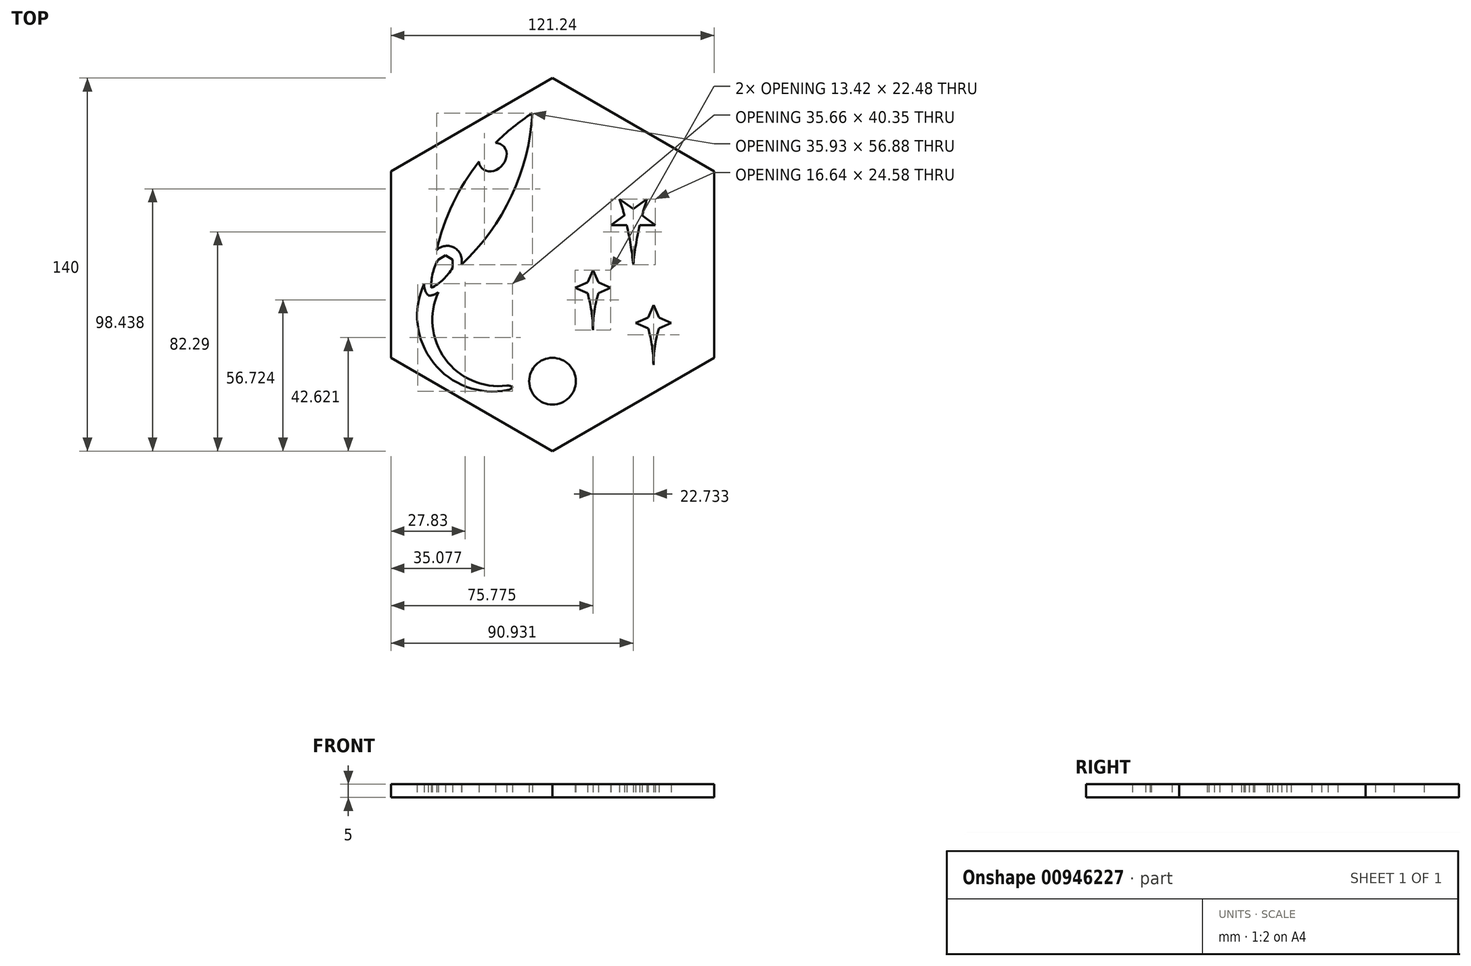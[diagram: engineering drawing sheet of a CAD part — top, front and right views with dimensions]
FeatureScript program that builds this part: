
annotation { "Feature Type Name" : "Feature", "Feature Type Description" : "" }
export const myFeature = defineFeature(function(context is Context, id is Id, definition is map)
    precondition{}
    {
        {
            var Q0;
            Q0=qCreatedBy(makeId("Top.planeOp"),FACE);
            var sketch = newSketch(context, id + "F0", { "sketchPlane" : qUnion([Q0])});
            skCircle(sketch, "E0.cCircle", {"center": v(0, 0) * mm, "radius": 60.62 * mm, "construction": true});
            skLineSegment(sketch, "E0.0", {"start": v(60.62, 35) * mm, "end": v(60.62, -35) * mm});
            skLineSegment(sketch, "E0.1", {"start": v(60.62, -35) * mm, "end": v(0, -70) * mm});
            skLineSegment(sketch, "E0.2", {"start": v(0, -70) * mm, "end": v(-60.62, -35) * mm});
            skLineSegment(sketch, "E0.3", {"start": v(-60.62, -35) * mm, "end": v(-60.62, 35) * mm});
            skLineSegment(sketch, "E0.4", {"start": v(-60.62, 35) * mm, "end": v(0, 70) * mm});
            skLineSegment(sketch, "E0.5", {"start": v(0, 70) * mm, "end": v(60.62, 35) * mm});
            skPoint(sketch, "E0.0.midPoint", {"position": v(60.62, 0) * mm});
            skLineSegment(sketch, "E1", {"start": v(0, 0) * mm, "end": v(0, -35) * mm, "construction": true});
            skLineSegment(sketch, "E2", {"start": v(-30.31, 17.5) * mm, "end": v(-60.62, 35) * mm, "construction": true});
            skLineSegment(sketch, "E3", {"start": v(0, 0) * mm, "end": v(60.62, 35) * mm, "construction": true});
            skLineSegment(sketch, "E4", {"start": v(60.62, -35) * mm, "end": v(15.16, -8.75) * mm, "construction": true});
            skLineSegment(sketch, "E5", {"start": v(0, -35) * mm, "end": v(30.31, 17.5) * mm, "construction": true});
            skLineSegment(sketch, "E6", {"start": v(0, -35) * mm, "end": v(0, -43.75) * mm, "construction": true});
            skLineSegment(sketch, "E7", {"start": v(0, -52.5) * mm, "end": v(0, -70) * mm, "construction": true});
            skLineSegment(sketch, "E8", {"start": v(0, -43.75) * mm, "end": v(0, -52.5) * mm, "construction": true});
            skCircle(sketch, "E9", {"center": v(0, -43.75) * mm, "radius": 8.75 * mm});
            skPoint(sketch, "E10", {"position": v(37.89, -21.88) * mm});
            skPoint(sketch, "E11", {"position": v(-30.31, 17.5) * mm});
            skLineSegment(sketch, "E12", {"start": v(-60.62, -35) * mm, "end": v(-45.47, -8.75) * mm, "construction": true});
            skLineSegment(sketch, "E13", {"start": v(0, 70) * mm, "end": v(-7.58, 56.88) * mm, "construction": true});
            skLineSegment(sketch, "E14", {"start": v(-45.47, -8.75) * mm, "end": v(-37.89, 4.37) * mm, "construction": true});
            skLineSegment(sketch, "E15", {"start": v(-15.16, 43.75) * mm, "end": v(-30.31, 17.5) * mm, "construction": true});
            skLineSegment(sketch, "E16", {"start": v(-7.58, 56.88) * mm, "end": v(-15.16, 43.75) * mm, "construction": true});
            skArc(sketch, "E17", {"start": v(-60.62, -16.52) * mm, "mid": v(-59.59, -16.11) * mm, "end": v(-58.56, -15.69) * mm, "construction": true});
            skLineSegment(sketch, "E18", {"start": v(-15.16, 8.75) * mm, "end": v(-30.31, 17.5) * mm, "construction": true});
            skLineSegment(sketch, "E19", {"start": v(0, 0) * mm, "end": v(-15.16, 8.75) * mm, "construction": true});
            skPoint(sketch, "E20", {"position": v(-22.73, 13.12) * mm});
            skArc(sketch, "E21.trimOffspring", {"start": v(-45.47, -8.75) * mm, "mid": v(-18.65, 19.52) * mm, "end": v(-7.58, 56.88) * mm});
            skArc(sketch, "E22.MirrorCS", {"start": v(-45.47, -8.75) * mm, "mid": v(-34.4, 28.6) * mm, "end": v(-7.58, 56.88) * mm});
            skLineSegment(sketch, "E23", {"start": v(-37.89, 4.37) * mm, "end": v(-34.1, 10.94) * mm, "construction": true});
            skLineSegment(sketch, "E24", {"start": v(-34.1, 10.94) * mm, "end": v(-30.31, 17.5) * mm, "construction": true});
            skCircle(sketch, "E25.cCircle", {"center": v(30.31, 17.5) * mm, "radius": 2.7 * mm, "construction": true});
            skLineSegment(sketch, "E25.0", {"start": v(35.45, 24.58) * mm, "end": v(30.31, 8.75) * mm});
            skLineSegment(sketch, "E25.1", {"start": v(38.63, 14.8) * mm, "end": v(21.99, 14.8) * mm});
            skLineSegment(sketch, "E25.2", {"start": v(30.31, 8.75) * mm, "end": v(25.17, 24.58) * mm});
            skLineSegment(sketch, "E25.3", {"start": v(21.99, 14.8) * mm, "end": v(35.45, 24.58) * mm});
            skLineSegment(sketch, "E25.4", {"start": v(25.17, 24.58) * mm, "end": v(38.63, 14.8) * mm});
            skPoint(sketch, "E25.0.midPoint", {"position": v(32.88, 16.66) * mm});
            skPoint(sketch, "E26.orphan", {"position": v(27.13, 18.53) * mm});
            skPoint(sketch, "E27.orphan", {"position": v(30.31, 20.84) * mm});
            skPoint(sketch, "E28.orphan", {"position": v(33.49, 18.53) * mm});
            skPoint(sketch, "E29.orphan", {"position": v(32.28, 14.8) * mm});
            skPoint(sketch, "E30.orphan", {"position": v(28.35, 14.8) * mm});
            skLineSegment(sketch, "E31", {"start": v(30.31, 17.5) * mm, "end": v(30.31, 0) * mm, "construction": true});
            skPoint(sketch, "E32", {"position": v(30.31, 8.75) * mm});
            skArc(sketch, "E33", {"start": v(30.31, 0) * mm, "mid": v(28.4, 12.43) * mm, "end": v(25.17, 24.58) * mm});
            skArc(sketch, "E34", {"start": v(35.45, 24.58) * mm, "mid": v(32.22, 12.43) * mm, "end": v(30.31, 0) * mm});
            skLineSegment(sketch, "E35", {"start": v(30.31, 17.5) * mm, "end": v(27.97, 18.85) * mm, "construction": true});
            skCircle(sketch, "E36", {"center": v(30.31, 17.5) * mm, "radius": 1.35 * mm, "construction": true});
            skPoint(sketch, "E37", {"position": v(29.14, 18.18) * mm});
            skCircle(sketch, "E38", {"center": v(30.31, 17.5) * mm, "radius": 2.03 * mm, "construction": true});
            skLineSegment(sketch, "E39", {"start": v(30.31, 17.5) * mm, "end": v(30.99, 18.67) * mm, "construction": true});
            skLineSegment(sketch, "E40", {"start": v(30.99, 18.67) * mm, "end": v(31.66, 19.84) * mm, "construction": true});
            skPoint(sketch, "E41", {"position": v(31.32, 19.26) * mm});
            skSolve(sketch);
        }
        {
            var Q0;
            Q0=qCreatedBy(makeId("Top.planeOp"),FACE);
            var sketch = newSketch(context, id + "F1", { "sketchPlane" : qUnion([Q0])});
            skPoint(sketch, "E42.0", {"position": v(15.16, -8.75) * mm});
            skLineSegment(sketch, "E43.0", {"start": v(0, -70) * mm, "end": v(-60.62, -35) * mm});
            skLineSegment(sketch, "E44.0", {"start": v(-60.62, -35) * mm, "end": v(-60.62, 35) * mm});
            skLineSegment(sketch, "E45.0", {"start": v(-60.62, 35) * mm, "end": v(0, 70) * mm});
            skLineSegment(sketch, "E46.0", {"start": v(0, 70) * mm, "end": v(60.62, 35) * mm});
            skLineSegment(sketch, "E47.0", {"start": v(60.62, 35) * mm, "end": v(60.62, -35) * mm});
            skLineSegment(sketch, "E48.0", {"start": v(60.62, -35) * mm, "end": v(0, -70) * mm});
            skArc(sketch, "E49.0", {"start": v(-45.47, -8.75) * mm, "mid": v(-18.65, 19.52) * mm, "end": v(-7.58, 56.88) * mm});
            skArc(sketch, "E50.0", {"start": v(-45.47, -8.75) * mm, "mid": v(-34.4, 28.6) * mm, "end": v(-7.58, 56.88) * mm});
            skCircle(sketch, "E51.cCircle", {"center": v(15.16, -8.75) * mm, "radius": 2.03 * mm, "construction": true});
            skLineSegment(sketch, "E51.3", {"start": v(13.13, -6.72) * mm, "end": v(17.18, -6.72) * mm});
            skPoint(sketch, "E51.0.midPoint", {"position": v(17.18, -8.75) * mm});
            skCircle(sketch, "E52.cCircle", {"center": v(15.16, -5.55) * mm, "radius": 1.17 * mm, "construction": true});
            skLineSegment(sketch, "E52.1", {"start": v(13.13, -6.72) * mm, "end": v(15.16, -3.2) * mm});
            skLineSegment(sketch, "E52.2", {"start": v(15.16, -3.2) * mm, "end": v(17.18, -6.72) * mm});
            skPoint(sketch, "E52.0.midPoint", {"position": v(15.16, -6.72) * mm});
            skLineSegment(sketch, "E53", {"start": v(15.16, -5.55) * mm, "end": v(15.16, -0.87) * mm, "construction": true});
            skPoint(sketch, "E54", {"position": v(15.16, -3.2) * mm});
            skLineSegment(sketch, "E55", {"start": v(15.16, -3.2) * mm, "end": v(15.16, -0.87) * mm, "construction": true});
            skLineSegment(sketch, "E56", {"start": v(17.18, -6.72) * mm, "end": v(15.16, -2.04) * mm});
            skLineSegment(sketch, "E57", {"start": v(13.13, -6.72) * mm, "end": v(15.16, -2.04) * mm});
            skLineSegment(sketch, "E58.1.0", {"start": v(13.13, -6.72) * mm, "end": v(8.44, -8.75) * mm});
            skPoint(sketch, "E58.1.1", {"position": v(13.13, -8.75) * mm});
            skLineSegment(sketch, "E58.1.2", {"start": v(9.62, -8.75) * mm, "end": v(13.13, -6.72) * mm});
            skLineSegment(sketch, "E58.1.3", {"start": v(9.62, -8.75) * mm, "end": v(7.27, -8.75) * mm, "construction": true});
            skLineSegment(sketch, "E58.1.4", {"start": v(11.96, -8.75) * mm, "end": v(7.27, -8.75) * mm, "construction": true});
            skLineSegment(sketch, "E58.1.5", {"start": v(13.13, -10.78) * mm, "end": v(8.44, -8.75) * mm});
            skLineSegment(sketch, "E58.1.6", {"start": v(13.13, -10.78) * mm, "end": v(13.13, -6.72) * mm});
            skCircle(sketch, "E58.1.7", {"center": v(11.96, -8.75) * mm, "radius": 1.17 * mm, "construction": true});
            skPoint(sketch, "E58.1.8", {"position": v(9.62, -8.75) * mm});
            skLineSegment(sketch, "E58.1.9", {"start": v(13.13, -10.78) * mm, "end": v(9.62, -8.75) * mm});
            skLineSegment(sketch, "E58.2.0", {"start": v(13.13, -10.78) * mm, "end": v(15.16, -15.46) * mm});
            skPoint(sketch, "E58.2.1", {"position": v(15.16, -10.78) * mm});
            skLineSegment(sketch, "E58.2.2", {"start": v(15.16, -14.3) * mm, "end": v(13.13, -10.78) * mm});
            skLineSegment(sketch, "E58.2.3", {"start": v(15.16, -14.3) * mm, "end": v(15.16, -16.63) * mm, "construction": true});
            skLineSegment(sketch, "E58.2.4", {"start": v(15.16, -11.95) * mm, "end": v(15.16, -16.63) * mm, "construction": true});
            skLineSegment(sketch, "E58.2.5", {"start": v(17.18, -10.78) * mm, "end": v(15.16, -15.46) * mm});
            skLineSegment(sketch, "E58.2.6", {"start": v(17.18, -10.78) * mm, "end": v(13.13, -10.78) * mm});
            skCircle(sketch, "E58.2.7", {"center": v(15.16, -11.95) * mm, "radius": 1.17 * mm, "construction": true});
            skPoint(sketch, "E58.2.8", {"position": v(15.16, -14.3) * mm});
            skLineSegment(sketch, "E58.2.9", {"start": v(17.18, -10.78) * mm, "end": v(15.16, -14.3) * mm});
            skLineSegment(sketch, "E58.3.0", {"start": v(17.18, -10.78) * mm, "end": v(21.87, -8.75) * mm});
            skLineSegment(sketch, "E58.3.2", {"start": v(20.7, -8.75) * mm, "end": v(17.18, -10.78) * mm});
            skLineSegment(sketch, "E58.3.3", {"start": v(20.7, -8.75) * mm, "end": v(23.04, -8.75) * mm, "construction": true});
            skLineSegment(sketch, "E58.3.4", {"start": v(18.35, -8.75) * mm, "end": v(23.04, -8.75) * mm, "construction": true});
            skLineSegment(sketch, "E58.3.5", {"start": v(17.18, -6.72) * mm, "end": v(21.87, -8.75) * mm});
            skLineSegment(sketch, "E58.3.6", {"start": v(17.18, -6.72) * mm, "end": v(17.18, -10.78) * mm});
            skCircle(sketch, "E58.3.7", {"center": v(18.35, -8.75) * mm, "radius": 1.17 * mm, "construction": true});
            skPoint(sketch, "E58.3.8", {"position": v(20.7, -8.75) * mm});
            skLineSegment(sketch, "E58.3.9", {"start": v(17.18, -6.72) * mm, "end": v(20.7, -8.75) * mm});
            skLineSegment(sketch, "E59", {"start": v(15.16, -8.75) * mm, "end": v(15.16, -24.51) * mm, "construction": true});
            skArc(sketch, "E60", {"start": v(17.18, -10.78) * mm, "mid": v(15.67, -17.57) * mm, "end": v(15.16, -24.51) * mm});
            skArc(sketch, "E61", {"start": v(15.16, -24.51) * mm, "mid": v(14.65, -17.57) * mm, "end": v(13.13, -10.78) * mm});
            skPoint(sketch, "E62.0", {"position": v(37.89, -21.88) * mm});
            skCircle(sketch, "E63.cCircle", {"center": v(37.89, -21.88) * mm, "radius": 2.03 * mm, "construction": true});
            skLineSegment(sketch, "E63.0", {"start": v(39.92, -19.85) * mm, "end": v(39.92, -23.9) * mm});
            skLineSegment(sketch, "E63.1", {"start": v(39.92, -23.9) * mm, "end": v(35.86, -23.9) * mm});
            skLineSegment(sketch, "E63.2", {"start": v(35.86, -23.9) * mm, "end": v(35.86, -19.85) * mm});
            skLineSegment(sketch, "E63.3", {"start": v(35.86, -19.85) * mm, "end": v(39.92, -19.85) * mm});
            skPoint(sketch, "E63.0.midPoint", {"position": v(39.92, -21.88) * mm});
            skCircle(sketch, "E64.cCircle", {"center": v(37.89, -18.68) * mm, "radius": 1.17 * mm, "construction": true});
            skLineSegment(sketch, "E64.0", {"start": v(35.86, -19.85) * mm, "end": v(37.89, -16.33) * mm});
            skLineSegment(sketch, "E64.1", {"start": v(37.89, -16.33) * mm, "end": v(39.92, -19.85) * mm});
            skLineSegment(sketch, "E64.2", {"start": v(39.92, -19.85) * mm, "end": v(35.86, -19.85) * mm});
            skPoint(sketch, "E64.0.midPoint", {"position": v(36.87, -18.1) * mm});
            skLineSegment(sketch, "E65", {"start": v(37.89, -18.68) * mm, "end": v(37.89, -14) * mm, "construction": true});
            skLineSegment(sketch, "E66", {"start": v(37.89, -16.33) * mm, "end": v(37.89, -14) * mm, "construction": true});
            skLineSegment(sketch, "E67", {"start": v(39.92, -19.85) * mm, "end": v(37.89, -15.16) * mm});
            skLineSegment(sketch, "E68", {"start": v(35.86, -19.85) * mm, "end": v(37.89, -15.16) * mm});
            skLineSegment(sketch, "E69.1.0", {"start": v(35.86, -23.9) * mm, "end": v(32.35, -21.87) * mm});
            skLineSegment(sketch, "E69.1.1", {"start": v(34.69, -21.87) * mm, "end": v(30, -21.88) * mm, "construction": true});
            skLineSegment(sketch, "E69.1.2", {"start": v(32.35, -21.88) * mm, "end": v(35.86, -19.85) * mm});
            skLineSegment(sketch, "E69.1.3", {"start": v(32.35, -21.88) * mm, "end": v(30, -21.88) * mm, "construction": true});
            skLineSegment(sketch, "E69.1.4", {"start": v(35.86, -23.9) * mm, "end": v(31.18, -21.88) * mm});
            skPoint(sketch, "E69.1.5", {"position": v(34.1, -22.89) * mm});
            skLineSegment(sketch, "E69.1.6", {"start": v(35.86, -19.85) * mm, "end": v(35.86, -23.9) * mm});
            skCircle(sketch, "E69.1.7", {"center": v(34.69, -21.87) * mm, "radius": 1.17 * mm, "construction": true});
            skLineSegment(sketch, "E69.1.8", {"start": v(35.86, -19.85) * mm, "end": v(31.18, -21.88) * mm});
            skLineSegment(sketch, "E69.2.0", {"start": v(39.92, -23.9) * mm, "end": v(37.89, -27.42) * mm});
            skLineSegment(sketch, "E69.2.1", {"start": v(37.89, -25.07) * mm, "end": v(37.89, -29.76) * mm, "construction": true});
            skLineSegment(sketch, "E69.2.2", {"start": v(37.89, -27.42) * mm, "end": v(35.86, -23.9) * mm});
            skLineSegment(sketch, "E69.2.3", {"start": v(37.89, -27.42) * mm, "end": v(37.89, -29.76) * mm, "construction": true});
            skLineSegment(sketch, "E69.2.4", {"start": v(39.92, -23.9) * mm, "end": v(37.89, -28.59) * mm});
            skPoint(sketch, "E69.2.5", {"position": v(38.9, -25.66) * mm});
            skLineSegment(sketch, "E69.2.6", {"start": v(35.86, -23.9) * mm, "end": v(39.92, -23.9) * mm});
            skCircle(sketch, "E69.2.7", {"center": v(37.89, -25.07) * mm, "radius": 1.17 * mm, "construction": true});
            skLineSegment(sketch, "E69.2.8", {"start": v(35.86, -23.9) * mm, "end": v(37.89, -28.59) * mm});
            skLineSegment(sketch, "E69.3.0", {"start": v(39.92, -19.85) * mm, "end": v(43.43, -21.88) * mm});
            skLineSegment(sketch, "E69.3.1", {"start": v(41.09, -21.88) * mm, "end": v(45.77, -21.87) * mm, "construction": true});
            skLineSegment(sketch, "E69.3.2", {"start": v(43.43, -21.87) * mm, "end": v(39.92, -23.9) * mm});
            skLineSegment(sketch, "E69.3.3", {"start": v(43.43, -21.87) * mm, "end": v(45.77, -21.87) * mm, "construction": true});
            skLineSegment(sketch, "E69.3.4", {"start": v(39.92, -19.85) * mm, "end": v(44.6, -21.88) * mm});
            skPoint(sketch, "E69.3.5", {"position": v(41.67, -20.86) * mm});
            skLineSegment(sketch, "E69.3.6", {"start": v(39.92, -23.9) * mm, "end": v(39.92, -19.85) * mm});
            skCircle(sketch, "E69.3.7", {"center": v(41.09, -21.88) * mm, "radius": 1.17 * mm, "construction": true});
            skLineSegment(sketch, "E69.3.8", {"start": v(39.92, -23.9) * mm, "end": v(44.6, -21.87) * mm});
            skLineSegment(sketch, "E70", {"start": v(37.89, -21.88) * mm, "end": v(37.89, -37.64) * mm, "construction": true});
            skSolve(sketch);
        }
        {
            var Q0;
            Q0=makeQuery(id+"F0.imprint","IMPRINT",FACE,{"disambiguationData":[TD([[makeQuery(id+"F0.imprint","IMPRINT",EDGE,{"derivedFrom":sQuery(id+"F0.wireOp",EDGE,"E0.0")}),-1.0]])]});
            var sketch = newSketch(context, id + "F2", { "sketchPlane" : qUnion([Q0])});
            skPoint(sketch, "E71.0", {"position": v(35.86, -23.9) * mm});
            skPoint(sketch, "E72.0", {"position": v(39.92, -23.9) * mm});
            skPoint(sketch, "E73.0", {"position": v(37.89, -37.64) * mm});
            skArc(sketch, "E74", {"start": v(37.89, -37.64) * mm, "mid": v(37.38, -30.7) * mm, "end": v(35.86, -23.9) * mm});
            skLineSegment(sketch, "E75.0", {"start": v(37.89, -21.88) * mm, "end": v(37.89, -37.64) * mm, "construction": true});
            skArc(sketch, "E76", {"start": v(39.92, -23.9) * mm, "mid": v(38.4, -30.7) * mm, "end": v(37.89, -37.64) * mm});
            skSolve(sketch);
        }
        {
            var Q0;
            Q0=makeQuery(id+"F0.imprint","IMPRINT",FACE,{"disambiguationData":[TD([[makeQuery(id+"F0.imprint","IMPRINT",EDGE,{"derivedFrom":sQuery(id+"F0.wireOp",EDGE,"E0.0")}),-1.0]])]});
            var sketch = newSketch(context, id + "F3", { "sketchPlane" : qUnion([Q0])});
            skArc(sketch, "E77.0", {"start": v(-43.5, 5.36) * mm, "mid": v(-30.57, 34.63) * mm, "end": v(-7.58, 56.88) * mm});
            skArc(sketch, "E77.1", {"start": v(-34.23, 0) * mm, "mid": v(-15.35, 25.84) * mm, "end": v(-7.58, 56.88) * mm});
            skArc(sketch, "E78", {"start": v(-34.23, 0) * mm, "mid": v(-36.78, 6.3) * mm, "end": v(-43.5, 5.36) * mm});
            skLineSegment(sketch, "E79", {"start": v(-34.23, 0) * mm, "end": v(-36.55, 1.34) * mm, "construction": true});
            skLineSegment(sketch, "E80", {"start": v(-38.87, 2.68) * mm, "end": v(-43.5, 5.36) * mm, "construction": true});
            skLineSegment(sketch, "E81", {"start": v(-36.55, 1.34) * mm, "end": v(-38.87, 2.68) * mm, "construction": true});
            skLineSegment(sketch, "E82", {"start": v(-38.87, 2.68) * mm, "end": v(-40.2, 0.36) * mm, "construction": true});
            skPoint(sketch, "E83.orphan", {"position": v(-45.47, -8.75) * mm});
            skCircle(sketch, "E84.cCircle", {"center": v(-40.2, 0.36) * mm, "radius": 2.68 * mm, "construction": true});
            skLineSegment(sketch, "E84.2", {"start": v(-42.89, 1.9) * mm, "end": v(-40.2, 3.45) * mm});
            skLineSegment(sketch, "E84.3", {"start": v(-40.2, 3.45) * mm, "end": v(-37.53, 1.9) * mm});
            skLineSegment(sketch, "E84.4", {"start": v(-37.53, 1.9) * mm, "end": v(-37.53, -1.19) * mm});
            skPoint(sketch, "E84.0.midPoint", {"position": v(-41.55, -1.96) * mm});
            skArc(sketch, "E85", {"start": v(-45.47, -8.75) * mm, "mid": v(-40.95, -5.54) * mm, "end": v(-37.53, -1.19) * mm});
            skArc(sketch, "E86.MirrorCS", {"start": v(-45.47, -8.75) * mm, "mid": v(-44.94, -3.24) * mm, "end": v(-42.89, 1.9) * mm});
            skLineSegment(sketch, "E87", {"start": v(-36.22, 1.9) * mm, "end": v(-42.37, -8.75) * mm, "construction": true});
            skLineSegment(sketch, "E88", {"start": v(-35.74, 1.9) * mm, "end": v(-41.9, -8.75) * mm, "construction": true});
            skCircle(sketch, "E89.0", {"center": v(0, -43.75) * mm, "radius": 8.75 * mm});
            skLineSegment(sketch, "E90", {"start": v(0, -43.75) * mm, "end": v(-8.75, -43.75) * mm, "construction": true});
            skLineSegment(sketch, "E91", {"start": v(-17.5, -43.75) * mm, "end": v(-8.75, -43.75) * mm, "construction": true});
            skPoint(sketch, "E92", {"position": v(-44.94, -3.24) * mm});
            skPoint(sketch, "E93", {"position": v(-40.95, -5.54) * mm});
            skLineSegment(sketch, "E94", {"start": v(-48.15, -7.2) * mm, "end": v(-45.47, -8.75) * mm, "construction": true});
            skLineSegment(sketch, "E95", {"start": v(-37.53, -1.19) * mm, "end": v(-42.79, -10.3) * mm, "construction": true});
            skLineSegment(sketch, "E96", {"start": v(0, -43.75) * mm, "end": v(0, -52.5) * mm, "construction": true});
            skLineSegment(sketch, "E97", {"start": v(0, -43.75) * mm, "end": v(-6.19, -49.94) * mm, "construction": true});
            skLineSegment(sketch, "E98", {"start": v(0, -52.5) * mm, "end": v(-8.75, -43.75) * mm, "construction": true});
            skPoint(sketch, "E99", {"position": v(-4.38, -48.13) * mm});
            skLineSegment(sketch, "E100", {"start": v(0, -43.75) * mm, "end": v(-16.17, -50.45) * mm, "construction": true});
            skLineSegment(sketch, "E101", {"start": v(-6.19, -49.94) * mm, "end": v(-8.75, -43.75) * mm, "construction": true});
            skPoint(sketch, "E102", {"position": v(-7.47, -46.84) * mm});
            skCircle(sketch, "E103", {"center": v(0, -43.75) * mm, "radius": 17.5 * mm, "construction": true});
            skLineSegment(sketch, "E104", {"start": v(-16.17, -50.45) * mm, "end": v(-16.83, -47.1) * mm, "construction": true});
            skPoint(sketch, "E105", {"position": v(-16.83, -47.1) * mm});
            skLineSegment(sketch, "E106", {"start": v(0, -43.75) * mm, "end": v(-12.63, -46.26) * mm, "construction": true});
            skLineSegment(sketch, "E107", {"start": v(-45.47, -8.75) * mm, "end": v(-44.94, -3.24) * mm, "construction": true});
            skLineSegment(sketch, "E108", {"start": v(-40.95, -5.54) * mm, "end": v(-45.47, -8.75) * mm, "construction": true});
            skPoint(sketch, "E109", {"position": v(-45.2, -6) * mm});
            skPoint(sketch, "E110", {"position": v(-43.2, -7.15) * mm});
            skLineSegment(sketch, "E111", {"start": v(-13.13, -43.75) * mm, "end": v(-12.63, -46.26) * mm, "construction": true});
            skPoint(sketch, "E112.0", {"position": v(-15.16, 43.75) * mm});
            skPoint(sketch, "E113.0", {"position": v(-30.31, 17.5) * mm});
            skLineSegment(sketch, "E114", {"start": v(-15.16, 43.75) * mm, "end": v(-18.94, 37.19) * mm, "construction": true});
            skLineSegment(sketch, "E115", {"start": v(-22.73, 30.62) * mm, "end": v(-30.31, 17.5) * mm, "construction": true});
            skLineSegment(sketch, "E116", {"start": v(-18.94, 37.19) * mm, "end": v(-22.73, 30.62) * mm, "construction": true});
            skEllipse(sketch, "E117", {"center": v(-22.42, 40.3) * mm, "majorRadius": 5.8 * mm, "minorRadius": 4.67 * mm, "majorAxis": v(0.67, 0.74)});
            skPoint(sketch, "E118", {"position": v(-26.3, 35.97) * mm});
            skPoint(sketch, "E119", {"position": v(-18.55, 44.63) * mm});
            skLineSegment(sketch, "E120", {"start": v(-7.58, 56.88) * mm, "end": v(-27.47, 31.17) * mm, "construction": true});
            skEllipse(sketch, "E121", {"center": v(-22.73, 30.62) * mm, "majorRadius": 8.74 * mm, "minorRadius": 3.79 * mm, "majorAxis": v(0.87, -0.5), "construction": true});
            skPoint(sketch, "E122", {"position": v(-24.63, 27.34) * mm});
            skPoint(sketch, "E123", {"position": v(-30.3, 35) * mm});
            skLineSegment(sketch, "E124", {"start": v(-30.3, 35) * mm, "end": v(-27.47, 31.17) * mm, "construction": true});
            skPoint(sketch, "E125", {"position": v(-27.47, 31.17) * mm});
            skPoint(sketch, "E126", {"position": v(-20.84, 33.9) * mm});
            skPoint(sketch, "E127", {"position": v(-25.9, 43.42) * mm});
            skLineSegment(sketch, "E128", {"start": v(-27.47, 31.17) * mm, "end": v(-24.63, 27.34) * mm, "construction": true});
            skPoint(sketch, "E129", {"position": v(-28.89, 33.08) * mm});
            skLineSegment(sketch, "E130", {"start": v(-7.58, 56.88) * mm, "end": v(-28.89, 33.08) * mm, "construction": true});
            skPoint(sketch, "E131", {"position": v(-18.94, 37.19) * mm});
            skLineSegment(sketch, "E132", {"start": v(-45.47, -8.75) * mm, "end": v(-42.79, -10.3) * mm, "construction": true});
            skLineSegment(sketch, "E133", {"start": v(-16.83, -47.1) * mm, "end": v(-17.5, -43.75) * mm, "construction": true});
            skPoint(sketch, "E134", {"position": v(-17.17, -45.42) * mm});
            skPoint(sketch, "E135", {"position": v(-12.88, -45) * mm});
            skLineSegment(sketch, "E136", {"start": v(-12.88, -45) * mm, "end": v(-17.17, -45.42) * mm, "construction": true});
            skLineSegment(sketch, "E137", {"start": v(-12.63, -46.26) * mm, "end": v(-17.16, -47.16) * mm, "construction": true});
            skLineSegment(sketch, "E138", {"start": v(-13.13, -43.75) * mm, "end": v(-17.5, -43.75) * mm, "construction": true});
            skPoint(sketch, "E139", {"position": v(-15.31, -43.75) * mm});
            skPoint(sketch, "E140", {"position": v(-14.9, -46.71) * mm});
            skLineSegment(sketch, "E141", {"start": v(-14.9, -46.71) * mm, "end": v(-15.02, -45.21) * mm, "construction": true});
            skPoint(sketch, "E142", {"position": v(-14.96, -45.96) * mm});
            skArc(sketch, "E143", {"start": v(-17.17, -45.42) * mm, "mid": v(-16.01, -45.5) * mm, "end": v(-14.96, -45.96) * mm});
            skArc(sketch, "E144", {"start": v(-16.83, -47.1) * mm, "mid": v(-15.8, -46.7) * mm, "end": v(-14.96, -45.96) * mm});
            skPoint(sketch, "E145", {"position": v(-40.3, -35.38) * mm});
            skLineSegment(sketch, "E146", {"start": v(-40.3, -35.38) * mm, "end": v(-43.78, -37.93) * mm, "construction": true});
            skPoint(sketch, "E147", {"position": v(-42.04, -36.66) * mm});
            skArc(sketch, "E148", {"start": v(-45.47, -8.75) * mm, "mid": v(-41.85, -36.9) * mm, "end": v(-14.96, -45.96) * mm, "construction": true});
            skLineSegment(sketch, "E149", {"start": v(-46.6, -11.63) * mm, "end": v(-45.47, -8.75) * mm, "construction": true});
            skLineSegment(sketch, "E150", {"start": v(-45.47, -8.75) * mm, "end": v(-46.49, -5.83) * mm, "construction": true});
            skArc(sketch, "E151", {"start": v(-48.15, -7.2) * mm, "mid": v(-44.74, -36.77) * mm, "end": v(-16.83, -47.1) * mm});
            skArc(sketch, "E152", {"start": v(-42.79, -10.3) * mm, "mid": v(-40.3, -35.38) * mm, "end": v(-17.17, -45.42) * mm});
            skArc(sketch, "E153", {"start": v(-48.15, -7.2) * mm, "mid": v(-47.84, -9.58) * mm, "end": v(-46.6, -11.63) * mm});
            skArc(sketch, "E154", {"start": v(-46.6, -11.63) * mm, "mid": v(-44.57, -11.3) * mm, "end": v(-42.79, -10.3) * mm});
            skSolve(sketch);
        }
        {
            var Q0;
            Q0=qCreatedBy(makeId("Top.planeOp"),FACE);
            var sketch = newSketch(context, id + "F4", { "sketchPlane" : qUnion([Q0])});
            skCircle(sketch, "E155.0", {"center": v(0, -43.75) * mm, "radius": 8.75 * mm});
            skLineSegment(sketch, "E156.0", {"start": v(60.62, -35) * mm, "end": v(0, -70) * mm});
            skLineSegment(sketch, "E157.0", {"start": v(60.62, 35) * mm, "end": v(60.62, -35) * mm});
            skLineSegment(sketch, "E158.0", {"start": v(0, 70) * mm, "end": v(60.62, 35) * mm});
            skLineSegment(sketch, "E159.0", {"start": v(-60.62, 35) * mm, "end": v(0, 70) * mm});
            skLineSegment(sketch, "E160.0", {"start": v(-60.62, -35) * mm, "end": v(-60.62, 35) * mm});
            skArc(sketch, "E161.0", {"start": v(-34.23, 0) * mm, "mid": v(-15.35, 25.84) * mm, "end": v(-7.58, 56.88) * mm});
            skArc(sketch, "E162.0", {"start": v(-43.5, 5.36) * mm, "mid": v(-37.41, 22.88) * mm, "end": v(-27.6, 38.63) * mm});
            skArc(sketch, "E163.0", {"start": v(-34.23, 0) * mm, "mid": v(-36.78, 6.3) * mm, "end": v(-43.5, 5.36) * mm});
            skLineSegment(sketch, "E164.0", {"start": v(-42.89, 1.9) * mm, "end": v(-40.2, 3.45) * mm});
            skArc(sketch, "E165.0", {"start": v(-45.47, -8.75) * mm, "mid": v(-44.94, -3.24) * mm, "end": v(-42.89, 1.9) * mm});
            skLineSegment(sketch, "E166.0", {"start": v(-40.2, 3.45) * mm, "end": v(-37.53, 1.9) * mm});
            skLineSegment(sketch, "E167.0", {"start": v(-37.53, 1.9) * mm, "end": v(-37.53, -1.19) * mm});
            skArc(sketch, "E168.0", {"start": v(-45.47, -8.75) * mm, "mid": v(-40.95, -5.54) * mm, "end": v(-37.53, -1.19) * mm});
            skArc(sketch, "E169.0", {"start": v(15.16, -24.51) * mm, "mid": v(14.65, -17.57) * mm, "end": v(13.13, -10.78) * mm});
            skArc(sketch, "E170.0", {"start": v(17.18, -10.78) * mm, "mid": v(15.67, -17.57) * mm, "end": v(15.16, -24.51) * mm});
            skLineSegment(sketch, "E171.0", {"start": v(17.18, -10.78) * mm, "end": v(21.87, -8.75) * mm});
            skLineSegment(sketch, "E172.0", {"start": v(17.18, -6.72) * mm, "end": v(21.87, -8.75) * mm});
            skLineSegment(sketch, "E173.0", {"start": v(17.18, -6.72) * mm, "end": v(15.16, -2.04) * mm});
            skLineSegment(sketch, "E174.0", {"start": v(13.13, -6.72) * mm, "end": v(15.16, -2.04) * mm});
            skLineSegment(sketch, "E175.0", {"start": v(13.13, -6.72) * mm, "end": v(8.44, -8.75) * mm});
            skLineSegment(sketch, "E176.0", {"start": v(13.13, -10.78) * mm, "end": v(8.44, -8.75) * mm});
            skArc(sketch, "E177.0", {"start": v(39.92, -23.9) * mm, "mid": v(38.4, -30.7) * mm, "end": v(37.89, -37.64) * mm});
            skArc(sketch, "E178.0", {"start": v(37.89, -37.64) * mm, "mid": v(37.38, -30.7) * mm, "end": v(35.86, -23.9) * mm});
            skLineSegment(sketch, "E179.0", {"start": v(35.86, -23.9) * mm, "end": v(31.18, -21.88) * mm});
            skLineSegment(sketch, "E180.0", {"start": v(35.86, -19.85) * mm, "end": v(31.18, -21.88) * mm});
            skLineSegment(sketch, "E181.0", {"start": v(35.86, -19.85) * mm, "end": v(37.89, -15.16) * mm});
            skLineSegment(sketch, "E182.0", {"start": v(39.92, -19.85) * mm, "end": v(37.89, -15.16) * mm});
            skLineSegment(sketch, "E183.0", {"start": v(39.92, -19.85) * mm, "end": v(44.6, -21.88) * mm});
            skLineSegment(sketch, "E184.0", {"start": v(39.92, -23.9) * mm, "end": v(44.6, -21.87) * mm});
            skLineSegment(sketch, "E185.0", {"start": v(21.99, 14.8) * mm, "end": v(26.98, 18.42) * mm});
            skLineSegment(sketch, "E186.0", {"start": v(25.17, 24.58) * mm, "end": v(30.31, 20.84) * mm});
            skArc(sketch, "E187.0", {"start": v(30.31, 0) * mm, "mid": v(29.33, 7.44) * mm, "end": v(27.88, 14.8) * mm});
            skArc(sketch, "E188.0", {"start": v(35.45, 24.58) * mm, "mid": v(34.5, 21.51) * mm, "end": v(33.64, 18.42) * mm});
            skLineSegment(sketch, "E189.0", {"start": v(38.63, 14.8) * mm, "end": v(32.74, 14.8) * mm});
            skLineSegment(sketch, "E190.trimOffspring", {"start": v(27.88, 14.8) * mm, "end": v(21.99, 14.8) * mm});
            skArc(sketch, "E191.trimOffspring", {"start": v(26.98, 18.42) * mm, "mid": v(26.12, 21.51) * mm, "end": v(25.17, 24.58) * mm});
            skLineSegment(sketch, "E192.trimOffspring", {"start": v(30.31, 20.84) * mm, "end": v(35.45, 24.58) * mm});
            skLineSegment(sketch, "E193.trimOffspring", {"start": v(33.64, 18.42) * mm, "end": v(38.63, 14.8) * mm});
            skArc(sketch, "E194.trimOffspring", {"start": v(32.74, 14.8) * mm, "mid": v(31.29, 7.44) * mm, "end": v(30.31, 0) * mm});
            skEllipticalArc(sketch, "E195.0", {});
            skArc(sketch, "E196.trimOffspring", {"start": v(-21.4, 45.63) * mm, "mid": v(-14.79, 51.62) * mm, "end": v(-7.58, 56.88) * mm});
            skArc(sketch, "E197.0", {"start": v(-17.17, -45.42) * mm, "mid": v(-16.01, -45.5) * mm, "end": v(-14.96, -45.96) * mm});
            skArc(sketch, "E198.0", {"start": v(-16.83, -47.1) * mm, "mid": v(-15.8, -46.7) * mm, "end": v(-14.96, -45.96) * mm});
            skLineSegment(sketch, "E199.0.0", {"start": v(60.62, 35) * mm, "end": v(0, 70) * mm});
            skLineSegment(sketch, "E199.0.1", {"start": v(0, 70) * mm, "end": v(-60.62, 35) * mm});
            skLineSegment(sketch, "E199.0.2", {"start": v(-60.62, 35) * mm, "end": v(-60.62, -35) * mm});
            skLineSegment(sketch, "E199.0.4", {"start": v(0, -70) * mm, "end": v(60.62, -35) * mm});
            skLineSegment(sketch, "E199.0.5", {"start": v(60.62, -35) * mm, "end": v(60.62, 35) * mm});
            skLineSegment(sketch, "E200.0.3", {"start": v(-60.62, -35) * mm, "end": v(0, -70) * mm});
            skArc(sketch, "E201.0", {"start": v(-48.15, -7.2) * mm, "mid": v(-44.74, -36.77) * mm, "end": v(-16.83, -47.1) * mm});
            skArc(sketch, "E202.0", {"start": v(-42.79, -10.3) * mm, "mid": v(-40.3, -35.38) * mm, "end": v(-17.17, -45.42) * mm});
            skArc(sketch, "E203.0", {"start": v(-48.15, -7.2) * mm, "mid": v(-47.84, -9.58) * mm, "end": v(-46.6, -11.63) * mm});
            skArc(sketch, "E204.0", {"start": v(-46.6, -11.63) * mm, "mid": v(-44.57, -11.3) * mm, "end": v(-42.79, -10.3) * mm});
            const initialGuessF4  = {"E195.0": [-0.022421108092777586, 0.040301324675147666, 0.6671519415157839, 0.7449216649633169, 0.005809593947329204, 0.004667339598941902, 2.51368173577678, 0.6416830810560054]};
            skSetInitialGuess(sketch, initialGuessF4);
            skSolve(sketch);
        }
        {
            var Q0;
            Q0=makeQuery(id+"F4.imprint","IMPRINT",FACE,{"disambiguationData":[TD([[makeQuery(id+"F4.imprint","IMPRINT",EDGE,{"derivedFrom":sQuery(id+"F4.wireOp",EDGE,"E155.0")}),-1.0]])]});
            extrude(context, id + "F5", {"entities" : qUnion([Q0]), "depth" : 5 * mm, "offsetDistance" : 25 * mm});
        }
    });
